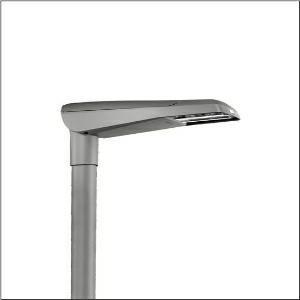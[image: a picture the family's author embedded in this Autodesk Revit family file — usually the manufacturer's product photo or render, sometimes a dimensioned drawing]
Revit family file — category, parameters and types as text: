
# Revit family: streetlight_sl_11_iq_micro___p1_0a_5xc1c51e08ce_6305
name_source: partatom
category: Lighting Fixtures
units: mm (PartAtom-declared; Revit-internal decimal feet)

## family parameters
Cut with Voids When Loaded = No
Host = Face
Light Source = No
Part Type = Normal
Room Calculation Point = No
Round Connector Dimension = Use Diameter
Shared = No

## types (1)
- --- (1 x LED, 1600 lm, 10.8 W, 3000K)
    Apparent Load = 11 VA
    CIE Flux Codes = 29 63 93 100 100
    Color Rendering = 70
    Color Temperature = 3000K
    Default Elevation = 1800 mm
    Description = Streetlight SL 11 iQ micro, mast luminaire, primary light control with 3 zone facetted reflector, of plastic, silver coated, highly specular, primary optical cover: cover, of PMMA, transparent, light distribution: P1.0a, light emission: direct distribution, primary light characteristic: asymmetric, installation type: post-top, side-entry, lamps: LED, High Power LED, rated values: 1.600lm | 10,8W | 148,1lm/W (begin service life); end service life: 1.600lm | 11,1W; at 50% lumin. flux: 800lm | 6W | 133,3lm/W, colour temperature: 3000K, colour rendering: CRI > 70, light colour: 730, light setting 1 begin service life: 100% | 1.600lm | 10,8W | 148,1lm/W | 3.000K, light setting 1 end service life: 11,1W, further light settings possible, control: optimised constant luminous flux control (CLO 2.0), Desk-Remote (wireless, voltage-free reading and setting of iQ features in the workshop via application-optimized NFC function/RFID function), Light-Fading, Smart-Wire, Night-Set, Lumen-Switch, Temp-Guard, Auto-Match, with cable H07RN-F 3x 1.5mm², mains connection: 230..240V, AC, 50/60Hz, connection cable pre-assembled, cable length: 5,5m, luminaire housing, of diecast aluminium, powder-coated, SITECO metallic grey (DB 702S), please order mast flange separately, inclination adjustable without tools: 0°, 5°, 10°, 15° (post-top) | 0°, -5°, -10°, -15° (side-entry), sealing non-destructively replaceable, multi-level sealing system, length: 600mm, width: 174mm, height: 116mm, mast flange for spigot size: 42mm (side-entry): 5XC10008XM4, 60/48mm (side-entry/post-top): 5XC10108XM2, 76/60mm (side-entry/post-top): 5XC10108XM1, equipment: standard, protection rating (complete): IP66, insulation class (complete): insulation class II (safety insulation), certification: CE, ENEC, ENEC+, VDE, impact resistance: IK10, permissible operating ambient temperature for outdoor applications: -25..+50°C, standard-compliant lighting for roads and squares, Environmental Product Declaration (EPD) tested and certified by an independent institute, packaging unit: 1 piece

Light Distribution: P1.0a
    Height = 116 mm
    Lamp = 1 x LED
    Lamp Light Flux = 1600 lm
    Lamp Power = 10.8 W
    Lamp count = 1
    Length = 600 mm
    Luminous efficacy = 148 lm/W
    Manufacturer = Siteco
    ModVariant = No
    Model = 5XC1C51E08CE
    Number of Poles = 1
    OnlyDefault = Yes
    Power Factor = 1
    Product Name = Streetlight SL 11 iQ micro | P1.0a
    Product group = mast luminaire | pylon top
    ProductGroupID = 6100
    Protection Class = Protection class II
    Protection Degree = IP 66
    RLX_Detail_Level = 1
    RLX_Emergency_Light_Flux = 0 lm
    RLX_Emergency_Type = 0
    RLX_Emergency_Type_DB = No
    RlxData = <blob elided: 26657 chars, md5=5e006c48>
    Socket = socket
    Standby Power = 0 W
    System Light Flux = 1600 lm
    System Power = 11 W
    Type Comments = factory setting: luminous flux: 100 % | dim-lin: 254 | 194 mA
    Type Image = l_1006566.jpg
    URL = http://relux.com
    VarID = @adj_019275
    Voltage = 0 V
    Weight = 0.00 kg
    Width = 174 mm

## geometry (parser evidence)
native form markers: Blend x4, Sweep x11
no freeform markers — native parametric forms only
